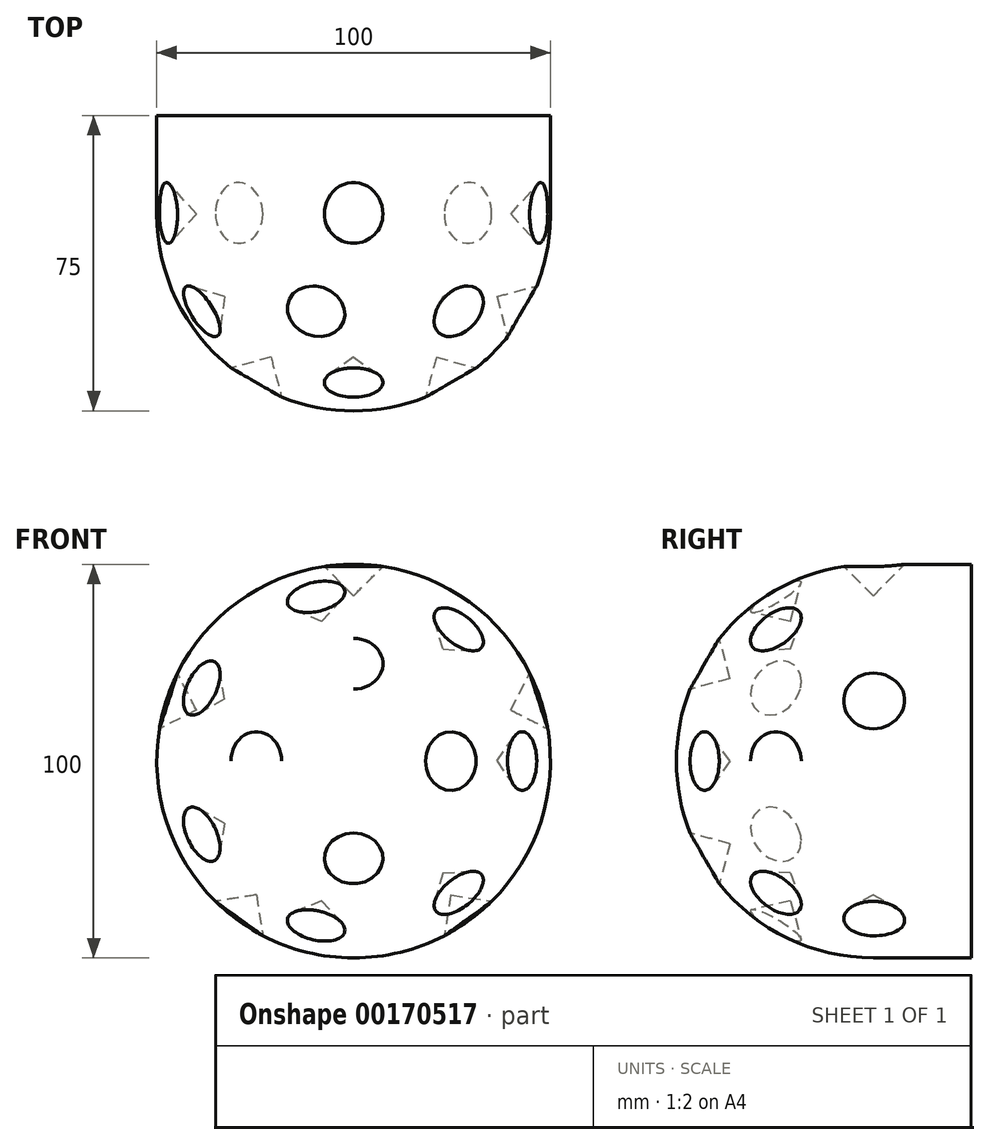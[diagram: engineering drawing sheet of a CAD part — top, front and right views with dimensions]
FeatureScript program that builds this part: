
annotation { "Feature Type Name" : "Feature", "Feature Type Description" : "" }
export const myFeature = defineFeature(function(context is Context, id is Id, definition is map)
    precondition{}
    {
        {
            var Q0;
            Q0=qCreatedBy(makeId("Front.planeOp"),FACE);
            var sketch = newSketch(context, id + "F0", { "sketchPlane" : qUnion([Q0])});
            skCircle(sketch, "E0", {"center": v(0, 0) * mm, "radius": 50 * mm});
            skSolve(sketch);
        }
        {
            var Q0;
            Q0 = qSketchRegion(id + "F0", true);
            extrude(context, id + "F1", {"entities" : qUnion([Q0]), "oppositeDirection" : true, "depth" : 25 * mm});
        }
        {
            var Q0;
            Q0=makeQuery(id+"F0.imprint","IMPRINT",FACE,{"disambiguationData":[TD([[makeQuery(id+"F0.imprint","IMPRINT",EDGE,{"derivedFrom":sQuery(id+"F0.wireOp",EDGE,"E0")}),1.0]])]});
            var sketch = newSketch(context, id + "F2", { "sketchPlane" : qUnion([Q0])});
            skArc(sketch, "E1.0", {"start": v(0, 50) * mm, "mid": v(-50, 0) * mm, "end": v(0, -50) * mm});
            skLineSegment(sketch, "E2", {"start": v(0, 50) * mm, "end": v(0, -50) * mm});
            skSolve(sketch);
        }
        {
            var Q0;
            Q0 = qSketchRegion(id + "F2", true);
            var Q1;
            Q1=sQuery(id+"F2.wireOp",EDGE,"E2");
            revolve(context, id + "F3", {"operationType" : NewBodyOperationType.ADD, "entities" : qUnion([Q0]), "axis" : qUnion([Q1]), "revolveType" : RevolveType.ONE_DIRECTION, "oppositeDirection" : true, "angle" : 180 * degree});
        }
        {
            var Q0;
            Q0=qCreatedBy(makeId("Right.planeOp"),FACE);
            var sketch = newSketch(context, id + "F4", { "sketchPlane" : qUnion([Q0])});
            skLineSegment(sketch, "E3", {"start": v(0, 52) * mm, "end": v(0, 42) * mm});
            skLineSegment(sketch, "E4", {"start": v(0, 42) * mm, "end": v(-10, 52) * mm});
            skLineSegment(sketch, "E5", {"start": v(-10, 52) * mm, "end": v(0, 52) * mm});
            skSolve(sketch);
        }
        {
            var Q0;
            Q0 = qSketchRegion(id + "F4", true);
            var Q1;
            Q1=sQuery(id+"F4.wireOp",EDGE,"E3");
            revolve(context, id + "F5", {"entities" : qUnion([Q0]), "axis" : qUnion([Q1]), "revolveType" : RevolveType.FULL});
        }
        {
            var Q0;
            Q0=makeQuery(id+"F5.opRevolve","SWEPT_BODY",BODY,{"disambiguationData":[OSD([sQuery(id+"F4.wireOp",EDGE,"E3"),sQuery(id+"F4.wireOp",EDGE,"E4"),sQuery(id+"F4.wireOp",EDGE,"E5")])]});
            var Q1;
            Q1=makeQuery(id+"F1.opExtrude","CAP_EDGE",EDGE,{"disambiguationData":[OSD([sQuery(id+"F0.wireOp",EDGE,"E0")])],"isStart":false});
            circularPattern(context, id + "F6", {"entities" : qUnion([Q0]), "axis" : qUnion([Q1]), "angle" : 360 * degree, "instanceCount" : 5, "equalSpace" : true});
        }
        {
            var Q0;
            Q0=makeQuery(id+"F5.opRevolve","SWEPT_BODY",BODY,{"disambiguationData":[OSD([sQuery(id+"F4.wireOp",EDGE,"E3"),sQuery(id+"F4.wireOp",EDGE,"E4"),sQuery(id+"F4.wireOp",EDGE,"E5")])]});
            var Q1;
            Q1=makeQuery(id+"F6.opPattern","COPY",BODY,{"derivedFrom":makeQuery(id+"F5.opRevolve","SWEPT_BODY",BODY,{"disambiguationData":[OSD([sQuery(id+"F4.wireOp",EDGE,"E3"),sQuery(id+"F4.wireOp",EDGE,"E4"),sQuery(id+"F4.wireOp",EDGE,"E5")])]}),"instanceName":"2"});
            var Q2;
            Q2=makeQuery(id+"F6.opPattern","COPY",BODY,{"derivedFrom":makeQuery(id+"F5.opRevolve","SWEPT_BODY",BODY,{"disambiguationData":[OSD([sQuery(id+"F4.wireOp",EDGE,"E3"),sQuery(id+"F4.wireOp",EDGE,"E4"),sQuery(id+"F4.wireOp",EDGE,"E5")])]}),"instanceName":"3"});
            var Q3;
            Q3=makeQuery(id+"F6.opPattern","COPY",BODY,{"derivedFrom":makeQuery(id+"F5.opRevolve","SWEPT_BODY",BODY,{"disambiguationData":[OSD([sQuery(id+"F4.wireOp",EDGE,"E3"),sQuery(id+"F4.wireOp",EDGE,"E4"),sQuery(id+"F4.wireOp",EDGE,"E5")])]}),"instanceName":"1"});
            var Q4;
            Q4=makeQuery(id+"F6.opPattern","COPY",BODY,{"derivedFrom":makeQuery(id+"F5.opRevolve","SWEPT_BODY",BODY,{"disambiguationData":[OSD([sQuery(id+"F4.wireOp",EDGE,"E3"),sQuery(id+"F4.wireOp",EDGE,"E4"),sQuery(id+"F4.wireOp",EDGE,"E5")])]}),"instanceName":"4"});
            var Q5;
            Q5=makeQuery(id+"F1.opExtrude","SWEPT_BODY",BODY,{"disambiguationData":[OSD([sQuery(id+"F0.wireOp",EDGE,"E0")])]});
            booleanBodies(context, id + "F7", {"operationType" : BooleanOperationType.SUBTRACTION, "tools" : qUnion([Q0, Q1, Q2, Q3, Q4]), "targets" : qUnion([Q5])});
        }
        {
            var Q0;
            Q0=qCreatedBy(makeId("Top.planeOp"),FACE);
            var sketch = newSketch(context, id + "F8", { "sketchPlane" : qUnion([Q0])});
            skLineSegment(sketch, "E6", {"start": v(45.03, -26) * mm, "end": v(40.03, -34.66) * mm});
            skLineSegment(sketch, "E7", {"start": v(40.03, -34.66) * mm, "end": v(36.37, -21) * mm});
            skLineSegment(sketch, "E8", {"start": v(36.37, -21) * mm, "end": v(45.03, -26) * mm});
            skSolve(sketch);
        }
        {
            var Q0;
            Q0 = qSketchRegion(id + "F8", true);
            var Q1;
            Q1=sQuery(id+"F8.wireOp",EDGE,"E8");
            revolve(context, id + "F9", {"entities" : qUnion([Q0]), "axis" : qUnion([Q1]), "revolveType" : RevolveType.FULL});
        }
        {
            var Q0;
            Q0=makeQuery(id+"F9.opRevolve","SWEPT_BODY",BODY,{"disambiguationData":[OSD([sQuery(id+"F8.wireOp",EDGE,"E6"),sQuery(id+"F8.wireOp",EDGE,"E7"),sQuery(id+"F8.wireOp",EDGE,"E8")])]});
            var Q1;
            Q1=makeQuery(id+"F1.opExtrude","CAP_EDGE",EDGE,{"disambiguationData":[OSD([sQuery(id+"F0.wireOp",EDGE,"E0")])],"isStart":false});
            circularPattern(context, id + "F10", {"entities" : qUnion([Q0]), "axis" : qUnion([Q1]), "angle" : 360 * degree, "instanceCount" : 7, "equalSpace" : true});
        }
        {
            var Q0;
            Q0=makeQuery(id+"F9.opRevolve","SWEPT_BODY",BODY,{"disambiguationData":[OSD([sQuery(id+"F8.wireOp",EDGE,"E6"),sQuery(id+"F8.wireOp",EDGE,"E7"),sQuery(id+"F8.wireOp",EDGE,"E8")])]});
            var Q1;
            Q1=makeQuery(id+"F10.opPattern","COPY",BODY,{"derivedFrom":makeQuery(id+"F9.opRevolve","SWEPT_BODY",BODY,{"disambiguationData":[OSD([sQuery(id+"F8.wireOp",EDGE,"E6"),sQuery(id+"F8.wireOp",EDGE,"E7"),sQuery(id+"F8.wireOp",EDGE,"E8")])]}),"instanceName":"1"});
            var Q2;
            Q2=makeQuery(id+"F10.opPattern","COPY",BODY,{"derivedFrom":makeQuery(id+"F9.opRevolve","SWEPT_BODY",BODY,{"disambiguationData":[OSD([sQuery(id+"F8.wireOp",EDGE,"E6"),sQuery(id+"F8.wireOp",EDGE,"E7"),sQuery(id+"F8.wireOp",EDGE,"E8")])]}),"instanceName":"2"});
            var Q3;
            Q3=makeQuery(id+"F10.opPattern","COPY",BODY,{"derivedFrom":makeQuery(id+"F9.opRevolve","SWEPT_BODY",BODY,{"disambiguationData":[OSD([sQuery(id+"F8.wireOp",EDGE,"E6"),sQuery(id+"F8.wireOp",EDGE,"E7"),sQuery(id+"F8.wireOp",EDGE,"E8")])]}),"instanceName":"3"});
            var Q4;
            Q4=makeQuery(id+"F10.opPattern","COPY",BODY,{"derivedFrom":makeQuery(id+"F9.opRevolve","SWEPT_BODY",BODY,{"disambiguationData":[OSD([sQuery(id+"F8.wireOp",EDGE,"E6"),sQuery(id+"F8.wireOp",EDGE,"E7"),sQuery(id+"F8.wireOp",EDGE,"E8")])]}),"instanceName":"4"});
            var Q5;
            Q5=makeQuery(id+"F10.opPattern","COPY",BODY,{"derivedFrom":makeQuery(id+"F9.opRevolve","SWEPT_BODY",BODY,{"disambiguationData":[OSD([sQuery(id+"F8.wireOp",EDGE,"E6"),sQuery(id+"F8.wireOp",EDGE,"E7"),sQuery(id+"F8.wireOp",EDGE,"E8")])]}),"instanceName":"5"});
            var Q6;
            Q6=makeQuery(id+"F10.opPattern","COPY",BODY,{"derivedFrom":makeQuery(id+"F9.opRevolve","SWEPT_BODY",BODY,{"disambiguationData":[OSD([sQuery(id+"F8.wireOp",EDGE,"E6"),sQuery(id+"F8.wireOp",EDGE,"E7"),sQuery(id+"F8.wireOp",EDGE,"E8")])]}),"instanceName":"6"});
            var Q7;
            Q7=makeQuery(id+"F1.opExtrude","SWEPT_BODY",BODY,{"disambiguationData":[OSD([sQuery(id+"F0.wireOp",EDGE,"E0")])]});
            booleanBodies(context, id + "F11", {"operationType" : BooleanOperationType.SUBTRACTION, "tools" : qUnion([Q0, Q1, Q2, Q3, Q4, Q5, Q6]), "targets" : qUnion([Q7])});
        }
        {
            var Q0;
            Q0=qCreatedBy(makeId("Right.planeOp"),FACE);
            var sketch = newSketch(context, id + "F12", { "sketchPlane" : qUnion([Q0])});
            skLineSegment(sketch, "E9", {"start": v(-45.03, 26) * mm, "end": v(-36.37, 21) * mm});
            skLineSegment(sketch, "E10", {"start": v(-36.37, 21) * mm, "end": v(-50.03, 17.34) * mm});
            skLineSegment(sketch, "E11", {"start": v(-50.03, 17.34) * mm, "end": v(-45.03, 26) * mm});
            skSolve(sketch);
        }
        {
            var Q0;
            Q0 = qSketchRegion(id + "F12", true);
            var Q1;
            Q1=sQuery(id+"F12.wireOp",EDGE,"E9");
            revolve(context, id + "F13", {"entities" : qUnion([Q0]), "axis" : qUnion([Q1]), "revolveType" : RevolveType.FULL});
        }
        {
            var Q0;
            Q0=makeQuery(id+"F13.opRevolve","SWEPT_BODY",BODY,{"disambiguationData":[OSD([sQuery(id+"F12.wireOp",EDGE,"E9"),sQuery(id+"F12.wireOp",EDGE,"E10"),sQuery(id+"F12.wireOp",EDGE,"E11")])]});
            var Q1;
            Q1=makeQuery(id+"F1.opExtrude","CAP_EDGE",EDGE,{"disambiguationData":[OSD([sQuery(id+"F0.wireOp",EDGE,"E0")])],"isStart":false});
            circularPattern(context, id + "F14", {"entities" : qUnion([Q0]), "axis" : qUnion([Q1]), "angle" : 360 * degree, "instanceCount" : 4, "equalSpace" : true});
        }
        {
            var Q0;
            Q0=makeQuery(id+"F14.opPattern","COPY",BODY,{"derivedFrom":makeQuery(id+"F13.opRevolve","SWEPT_BODY",BODY,{"disambiguationData":[OSD([sQuery(id+"F12.wireOp",EDGE,"E9"),sQuery(id+"F12.wireOp",EDGE,"E10"),sQuery(id+"F12.wireOp",EDGE,"E11")])]}),"instanceName":"1"});
            var Q1;
            Q1=makeQuery(id+"F14.opPattern","COPY",BODY,{"derivedFrom":makeQuery(id+"F13.opRevolve","SWEPT_BODY",BODY,{"disambiguationData":[OSD([sQuery(id+"F12.wireOp",EDGE,"E9"),sQuery(id+"F12.wireOp",EDGE,"E10"),sQuery(id+"F12.wireOp",EDGE,"E11")])]}),"instanceName":"2"});
            var Q2;
            Q2=makeQuery(id+"F14.opPattern","COPY",BODY,{"derivedFrom":makeQuery(id+"F13.opRevolve","SWEPT_BODY",BODY,{"disambiguationData":[OSD([sQuery(id+"F12.wireOp",EDGE,"E9"),sQuery(id+"F12.wireOp",EDGE,"E10"),sQuery(id+"F12.wireOp",EDGE,"E11")])]}),"instanceName":"3"});
            var Q3;
            Q3=makeQuery(id+"F13.opRevolve","SWEPT_BODY",BODY,{"disambiguationData":[OSD([sQuery(id+"F12.wireOp",EDGE,"E9"),sQuery(id+"F12.wireOp",EDGE,"E10"),sQuery(id+"F12.wireOp",EDGE,"E11")])]});
            var Q4;
            Q4=makeQuery(id+"F1.opExtrude","SWEPT_BODY",BODY,{"disambiguationData":[OSD([sQuery(id+"F0.wireOp",EDGE,"E0")])]});
            booleanBodies(context, id + "F15", {"operationType" : BooleanOperationType.SUBTRACTION, "tools" : qUnion([Q0, Q1, Q2, Q3]), "targets" : qUnion([Q4])});
        }
    });
